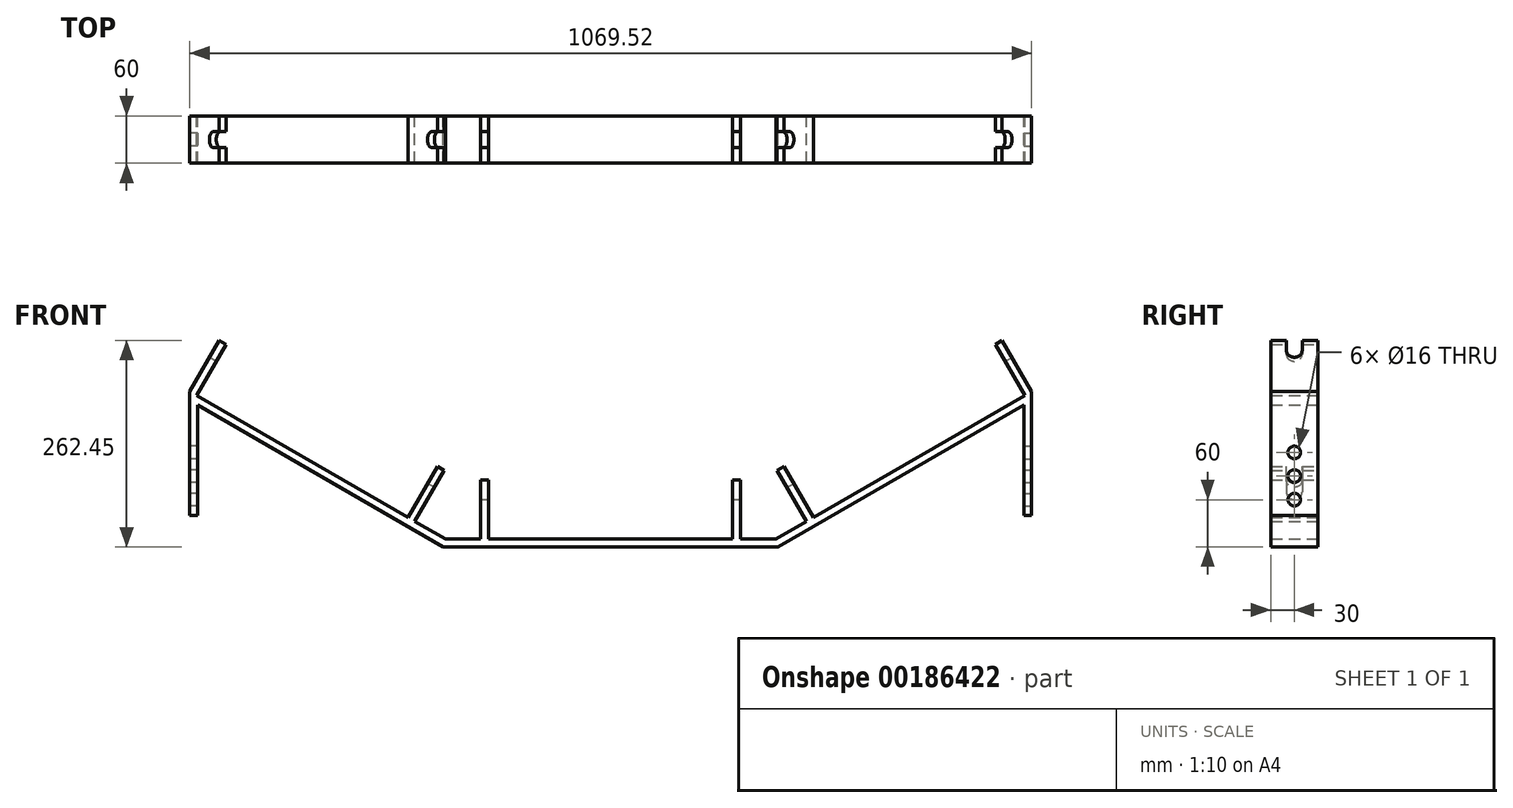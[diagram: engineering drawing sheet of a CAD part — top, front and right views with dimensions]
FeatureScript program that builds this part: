
annotation { "Feature Type Name" : "Feature", "Feature Type Description" : "" }
export const myFeature = defineFeature(function(context is Context, id is Id, definition is map)
    precondition{}
    {
        {
            var Q0;
            Q0=qCreatedBy(makeId("Front.planeOp"),FACE);
            var sketch = newSketch(context, id + "F0", { "sketchPlane" : qUnion([Q0])});
            skLineSegment(sketch, "E0", {"start": v(210, 10) * mm, "end": v(534.76, 197.5) * mm});
            skLineSegment(sketch, "E1", {"start": v(155, 10) * mm, "end": v(155, 85) * mm});
            skLineSegment(sketch, "E2", {"start": v(155, 85) * mm, "end": v(165, 85) * mm});
            skLineSegment(sketch, "E3", {"start": v(165, 85) * mm, "end": v(165, 10) * mm});
            skLineSegment(sketch, "E4", {"start": v(165, 10) * mm, "end": v(155, 10) * mm});
            skLineSegment(sketch, "E5", {"start": v(248.97, 32.5) * mm, "end": v(211.47, 97.45) * mm});
            skLineSegment(sketch, "E6", {"start": v(211.47, 97.45) * mm, "end": v(220.13, 102.45) * mm});
            skLineSegment(sketch, "E7", {"start": v(220.13, 102.45) * mm, "end": v(257.63, 37.5) * mm});
            skLineSegment(sketch, "E8", {"start": v(257.63, 37.5) * mm, "end": v(248.97, 32.5) * mm});
            skLineSegment(sketch, "E9", {"start": v(534.76, 197.5) * mm, "end": v(497.26, 262.45) * mm});
            skLineSegment(sketch, "E10", {"start": v(497.26, 262.45) * mm, "end": v(488.6, 257.45) * mm});
            skLineSegment(sketch, "E11", {"start": v(488.6, 257.45) * mm, "end": v(526.1, 192.5) * mm});
            skLineSegment(sketch, "E12", {"start": v(526.1, 192.5) * mm, "end": v(534.76, 197.5) * mm});
            skLineSegment(sketch, "E13", {"start": v(534.76, 197.5) * mm, "end": v(534.76, 40) * mm});
            skLineSegment(sketch, "E14", {"start": v(534.76, 40) * mm, "end": v(524.76, 40) * mm});
            skLineSegment(sketch, "E15", {"start": v(524.76, 40) * mm, "end": v(524.76, 180.18) * mm});
            skLineSegment(sketch, "E16", {"start": v(524.76, 180.18) * mm, "end": v(212.68, 0) * mm});
            skLineSegment(sketch, "E17", {"start": v(212.68, 0) * mm, "end": v(0, 0) * mm});
            skLineSegment(sketch, "E18", {"start": v(0, 10) * mm, "end": v(210, 10) * mm});
            skLineSegment(sketch, "E19", {"start": v(0, 10) * mm, "end": v(0, 0) * mm});
            skLineSegment(sketch, "E20.MirrorCS", {"start": v(0, 10) * mm, "end": v(-210, 10) * mm});
            skLineSegment(sketch, "E21.MirrorCS", {"start": v(-212.68, 0) * mm, "end": v(0, 0) * mm});
            skLineSegment(sketch, "E22.MirrorCS", {"start": v(-155, 10) * mm, "end": v(-155, 85) * mm});
            skLineSegment(sketch, "E23.MirrorCS", {"start": v(-165, 85) * mm, "end": v(-165, 10) * mm});
            skLineSegment(sketch, "E24.MirrorCS", {"start": v(-155, 85) * mm, "end": v(-165, 85) * mm});
            skLineSegment(sketch, "E25.MirrorCS", {"start": v(-248.97, 32.5) * mm, "end": v(-211.47, 97.45) * mm});
            skLineSegment(sketch, "E26.MirrorCS", {"start": v(-220.13, 102.45) * mm, "end": v(-257.63, 37.5) * mm});
            skLineSegment(sketch, "E27.MirrorCS", {"start": v(-210, 10) * mm, "end": v(-534.76, 197.5) * mm});
            skLineSegment(sketch, "E28.MirrorCS", {"start": v(-524.76, 180.18) * mm, "end": v(-212.68, 0) * mm});
            skLineSegment(sketch, "E29.MirrorCS", {"start": v(-488.6, 257.45) * mm, "end": v(-526.1, 192.5) * mm});
            skLineSegment(sketch, "E30.MirrorCS", {"start": v(-534.76, 197.5) * mm, "end": v(-497.26, 262.45) * mm});
            skLineSegment(sketch, "E31.MirrorCS", {"start": v(-524.76, 40) * mm, "end": v(-524.76, 180.18) * mm});
            skLineSegment(sketch, "E32.MirrorCS", {"start": v(-534.76, 197.5) * mm, "end": v(-534.76, 40) * mm});
            skLineSegment(sketch, "E33.MirrorCS", {"start": v(-534.76, 40) * mm, "end": v(-524.76, 40) * mm});
            skLineSegment(sketch, "E34.MirrorCS", {"start": v(-211.47, 97.45) * mm, "end": v(-220.13, 102.45) * mm});
            skLineSegment(sketch, "E35.MirrorCS", {"start": v(-497.26, 262.45) * mm, "end": v(-488.6, 257.45) * mm});
            skSolve(sketch);
        }
        {
            var Q0;
            Q0 = qSketchRegion(id + "F0", true);
            extrude(context, id + "F1", {"entities" : qUnion([Q0]), "depth" : 60 * mm});
        }
        {
            var Q0;
            Q0=makeQuery(id+"F1.opExtrude","SWEPT_FACE",FACE,{"disambiguationData":[OSD([sQuery(id+"F0.wireOp",EDGE,"E30.MirrorCS")])]});
            var sketch = newSketch(context, id + "F2", { "sketchPlane" : qUnion([Q0])});
            skLineSegment(sketch, "E36", {"start": v(20, -21.34) * mm, "end": v(20, -36.34) * mm});
            skLineSegment(sketch, "E37", {"start": v(20, -36.34) * mm, "end": v(20, -21.34) * mm});
            skLineSegment(sketch, "E38", {"start": v(40, -21.34) * mm, "end": v(40, -36.34) * mm});
            skArc(sketch, "E39", {"start": v(20, -36.34) * mm, "mid": v(30, -46.34) * mm, "end": v(40, -36.34) * mm});
            skLineSegment(sketch, "E40", {"start": v(40, -21.34) * mm, "end": v(20, -21.34) * mm});
            skPoint(sketch, "E41", {"position": v(30, -21.34) * mm});
            skSolve(sketch);
        }
        {
            var Q0;
            Q0 = qSketchRegion(id + "F2", true);
            var Q1;
            Q1=makeQuery(id+"F1.opExtrude","SWEPT_FACE",FACE,{"disambiguationData":[OSD([sQuery(id+"F0.wireOp",EDGE,"E25.MirrorCS")])]});
            extrude(context, id + "F3", {"entities" : qUnion([Q0]), "operationType" : NewBodyOperationType.REMOVE, "endBound" : BoundingType.UP_TO_SURFACE, "oppositeDirection" : true, "endBoundEntityFace" : qUnion([Q1]), "depth" : 25 * mm});
        }
        {
            var Q0;
            Q0=makeQuery(id+"F1.opExtrude","SWEPT_FACE",FACE,{"disambiguationData":[OSD([sQuery(id+"F0.wireOp",EDGE,"E23.MirrorCS")])]});
            var sketch = newSketch(context, id + "F4", { "sketchPlane" : qUnion([Q0])});
            skLineSegment(sketch, "E42", {"start": v(40, 85) * mm, "end": v(40, 70) * mm});
            skLineSegment(sketch, "E43", {"start": v(40, 70) * mm, "end": v(40, 85) * mm});
            skLineSegment(sketch, "E44", {"start": v(20, 85) * mm, "end": v(20, 70) * mm});
            skLineSegment(sketch, "E45", {"start": v(20, 70) * mm, "end": v(20, 85) * mm});
            skLineSegment(sketch, "E46", {"start": v(40, 85) * mm, "end": v(20, 85) * mm});
            skArc(sketch, "E47", {"start": v(20, 70) * mm, "mid": v(30, 60) * mm, "end": v(40, 70) * mm});
            skPoint(sketch, "E48", {"position": v(30, 85) * mm});
            skSolve(sketch);
        }
        {
            var Q0;
            Q0 = qSketchRegion(id + "F4", true);
            var Q1;
            Q1=makeQuery(id+"F1.opExtrude","SWEPT_FACE",FACE,{"disambiguationData":[OSD([sQuery(id+"F0.wireOp",EDGE,"E3")])]});
            extrude(context, id + "F5", {"entities" : qUnion([Q0]), "operationType" : NewBodyOperationType.REMOVE, "endBound" : BoundingType.UP_TO_SURFACE, "oppositeDirection" : true, "endBoundEntityFace" : qUnion([Q1]), "depth" : 25 * mm});
        }
        {
            var Q0;
            Q0=makeQuery(id+"F1.opExtrude","SWEPT_FACE",FACE,{"disambiguationData":[OSD([sQuery(id+"F0.wireOp",EDGE,"E9")])]});
            var sketch = newSketch(context, id + "F6", { "sketchPlane" : qUnion([Q0])});
            skLineSegment(sketch, "E49", {"start": v(-40, -36.34) * mm, "end": v(-40, -21.34) * mm});
            skLineSegment(sketch, "E50", {"start": v(-40, -21.34) * mm, "end": v(-20, -21.34) * mm});
            skLineSegment(sketch, "E51", {"start": v(-20, -21.34) * mm, "end": v(-20, -36.34) * mm});
            skArc(sketch, "E52", {"start": v(-40, -36.34) * mm, "mid": v(-30, -46.34) * mm, "end": v(-20, -36.34) * mm});
            skPoint(sketch, "E53", {"position": v(-30, -21.34) * mm});
            skSolve(sketch);
        }
        {
            var Q0;
            Q0 = qSketchRegion(id + "F6", true);
            var Q1;
            Q1=makeQuery(id+"F1.opExtrude","SWEPT_FACE",FACE,{"disambiguationData":[OSD([sQuery(id+"F0.wireOp",EDGE,"E5")])]});
            extrude(context, id + "F7", {"entities" : qUnion([Q0]), "operationType" : NewBodyOperationType.REMOVE, "endBound" : BoundingType.UP_TO_SURFACE, "oppositeDirection" : true, "endBoundEntityFace" : qUnion([Q1]), "depth" : 25 * mm});
        }
        {
            var Q0;
            Q0=makeQuery(id+"F1.opExtrude","SWEPT_FACE",FACE,{"disambiguationData":[OSD([sQuery(id+"F0.wireOp",EDGE,"E32.MirrorCS")])]});
            var sketch = newSketch(context, id + "F8", { "sketchPlane" : qUnion([Q0])});
            skCircle(sketch, "E54", {"center": v(30, 60) * mm, "radius": 8 * mm});
            skPoint(sketch, "E54.centerSnap0", {"position": v(30, 40) * mm});
            skCircle(sketch, "E55", {"center": v(30, 120) * mm, "radius": 8 * mm});
            skCircle(sketch, "E56", {"center": v(30, 90) * mm, "radius": 8 * mm});
            skSolve(sketch);
        }
        {
            var Q0;
            Q0 = qSketchRegion(id + "F8", true);
            var Q1;
            Q1=makeQuery(id+"F1.opExtrude","SWEPT_FACE",FACE,{"disambiguationData":[OSD([sQuery(id+"F0.wireOp",EDGE,"E13")])]});
            extrude(context, id + "F9", {"entities" : qUnion([Q0]), "operationType" : NewBodyOperationType.REMOVE, "oppositeDirection" : true, "endBoundEntityFace" : qUnion([Q1]), "depth" : 25 * mm});
        }
        {
            var Q0;
            Q0=makeQuery(id+"F1.opExtrude","SWEPT_FACE",FACE,{"disambiguationData":[OSD([sQuery(id+"F0.wireOp",EDGE,"E13")])]});
            var sketch = newSketch(context, id + "F10", { "sketchPlane" : qUnion([Q0])});
            skCircle(sketch, "E57", {"center": v(-30, 60) * mm, "radius": 8 * mm});
            skPoint(sketch, "E57.centerSnap0", {"position": v(-30, 40) * mm});
            skCircle(sketch, "E58", {"center": v(-30, 120) * mm, "radius": 8 * mm});
            skCircle(sketch, "E59", {"center": v(-30, 90) * mm, "radius": 8 * mm});
            skSolve(sketch);
        }
        {
            var Q0;
            Q0 = qSketchRegion(id + "F10", true);
            extrude(context, id + "F11", {"entities" : qUnion([Q0]), "operationType" : NewBodyOperationType.REMOVE, "oppositeDirection" : true, "depth" : 25 * mm});
        }
    });
